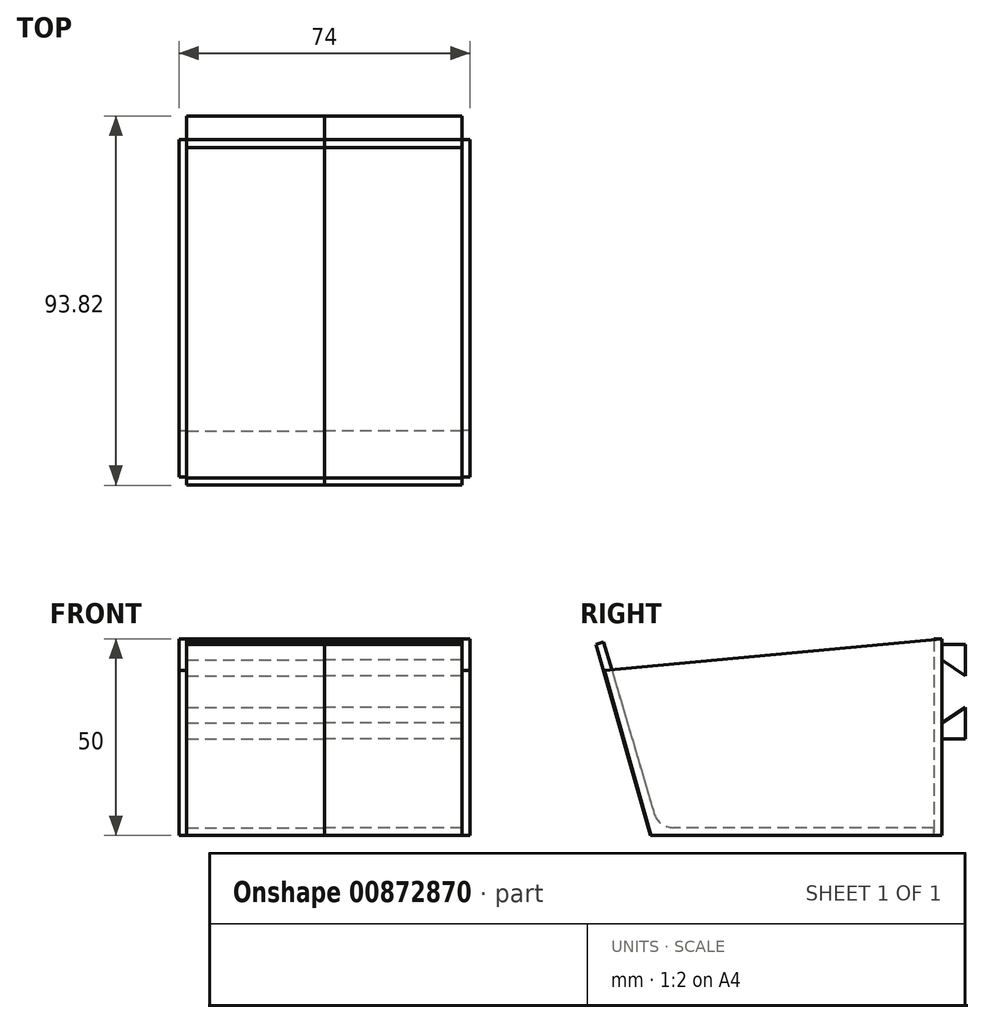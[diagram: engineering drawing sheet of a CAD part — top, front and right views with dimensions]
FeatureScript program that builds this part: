
annotation { "Feature Type Name" : "Feature", "Feature Type Description" : "" }
export const myFeature = defineFeature(function(context is Context, id is Id, definition is map)
    precondition{}
    {
        {
            var Q0;
            Q0=qCreatedBy(makeId("Front.planeOp"),FACE);
            var sketch = newSketch(context, id + "F0", { "sketchPlane" : qUnion([Q0])});
            skLineSegment(sketch, "E0.bottom", {"start": v(-35, 37.16) * mm, "end": v(0, 37.16) * mm});
            skLineSegment(sketch, "E0.top", {"start": v(-35, -12.84) * mm, "end": v(0, -12.84) * mm});
            skLineSegment(sketch, "E0.left", {"start": v(-35, 37.16) * mm, "end": v(-35, -12.84) * mm});
            skLineSegment(sketch, "E0.right", {"start": v(0, 37.16) * mm, "end": v(0, -12.84) * mm});
            skSolve(sketch);
        }
        {
            var Q0;
            Q0=makeQuery(id+"F0.imprint","IMPRINT",FACE,{"disambiguationData":[TD([[makeQuery(id+"F0.imprint","IMPRINT",EDGE,{"derivedFrom":sQuery(id+"F0.wireOp",EDGE,"E0.bottom")}),-1.0]])]});
            extrude(context, id + "F1", {"entities" : qUnion([Q0]), "depth" : 2 * mm, "offsetDistance" : 25 * mm});
        }
        {
            var Q0;
            Q0=qCreatedBy(makeId("Right.planeOp"),FACE);
            var sketch = newSketch(context, id + "F2", { "sketchPlane" : qUnion([Q0])});
            skLineSegment(sketch, "E1", {"start": v(0, 35.71) * mm, "end": v(6, 35.71) * mm});
            skLineSegment(sketch, "E2", {"start": v(6, 35.71) * mm, "end": v(6, 27.71) * mm});
            skLineSegment(sketch, "E3", {"start": v(6, 27.71) * mm, "end": v(0, 31.71) * mm});
            skLineSegment(sketch, "E4", {"start": v(6, 19.71) * mm, "end": v(6, 11.71) * mm});
            skLineSegment(sketch, "E5", {"start": v(6, 11.71) * mm, "end": v(0, 11.71) * mm});
            skLineSegment(sketch, "E6", {"start": v(6, 19.71) * mm, "end": v(0, 15.71) * mm});
            skLineSegment(sketch, "E7", {"start": v(0, 35.71) * mm, "end": v(0, 31.71) * mm});
            skLineSegment(sketch, "E8", {"start": v(0, 15.71) * mm, "end": v(0, 11.71) * mm});
            skLineSegment(sketch, "E9.bottom", {"start": v(-2, -12.84) * mm, "end": v(-72, -12.84) * mm});
            skLineSegment(sketch, "E9.top", {"start": v(-2, -10.84) * mm, "end": v(-68.26, -10.84) * mm});
            skLineSegment(sketch, "E9.left", {"start": v(-2, -12.84) * mm, "end": v(-2, -10.84) * mm});
            skLineSegment(sketch, "E9.right", {"start": v(-72, -12.84) * mm, "end": v(-72, -10.84) * mm});
            skLineSegment(sketch, "E10", {"start": v(-87.82, 35.71) * mm, "end": v(-85.91, 36.33) * mm});
            skLineSegment(sketch, "E11", {"start": v(-85.91, 36.33) * mm, "end": v(-73.06, -7.26) * mm});
            skLineSegment(sketch, "E12", {"start": v(-72, -12.84) * mm, "end": v(-74, -12.84) * mm});
            skLineSegment(sketch, "E13", {"start": v(-87.82, 35.71) * mm, "end": v(-74, -12.84) * mm});
            skPoint(sketch, "E14.visualSharp", {"position": v(-72, -10.84) * mm});
            skArc(sketch, "E14.filletArc", {"start": v(-73.06, -7.26) * mm, "mid": v(-71.26, -9.85) * mm, "end": v(-68.26, -10.84) * mm});
            skSolve(sketch);
        }
        {
            var Q0;
            Q0 = qSketchRegion(id + "F2", true);
            extrude(context, id + "F3", {"entities" : qUnion([Q0]), "oppositeDirection" : true, "depth" : 35 * mm, "offsetDistance" : 25 * mm});
        }
        {
            var Q0;
            Q0=makeQuery(id+"F1.opExtrude","SWEPT_FACE",FACE,{"disambiguationData":[OSD([sQuery(id+"F0.wireOp",EDGE,"E0.left")])]});
            var sketch = newSketch(context, id + "F4", { "sketchPlane" : qUnion([Q0])});
            skLineSegment(sketch, "E15", {"start": v(0, 37.16) * mm, "end": v(0, -12.84) * mm});
            skLineSegment(sketch, "E16", {"start": v(0, -12.84) * mm, "end": v(73.88, -12.84) * mm});
            skLineSegment(sketch, "E17", {"start": v(73.88, -12.84) * mm, "end": v(85.68, 29.12) * mm});
            skLineSegment(sketch, "E18", {"start": v(85.68, 29.12) * mm, "end": v(0, 37.16) * mm});
            skSolve(sketch);
        }
        {
            var Q0;
            Q0 = qSketchRegion(id + "F4", true);
            extrude(context, id + "F5", {"entities" : qUnion([Q0]), "depth" : 2 * mm, "offsetDistance" : 25 * mm});
        }
        {
            var Q0;
            Q0=makeQuery(id+"F5.opExtrude","SWEPT_BODY",BODY,{"disambiguationData":[OSD([sQuery(id+"F4.wireOp",EDGE,"E15"),sQuery(id+"F4.wireOp",EDGE,"E16"),sQuery(id+"F4.wireOp",EDGE,"E17"),sQuery(id+"F4.wireOp",EDGE,"E18")])]});
            var Q1;
            Q1=makeQuery(id+"F3.opExtrude","SWEPT_BODY",BODY,{"disambiguationData":[OSD([sQuery(id+"F2.wireOp",EDGE,"E4"),sQuery(id+"F2.wireOp",EDGE,"E5"),sQuery(id+"F2.wireOp",EDGE,"E6"),sQuery(id+"F2.wireOp",EDGE,"E8")])]});
            var Q2;
            Q2=makeQuery(id+"F3.opExtrude","SWEPT_BODY",BODY,{"disambiguationData":[OSD([sQuery(id+"F2.wireOp",EDGE,"E9.bottom"),sQuery(id+"F2.wireOp",EDGE,"E9.top"),sQuery(id+"F2.wireOp",EDGE,"E9.left"),sQuery(id+"F2.wireOp",EDGE,"E10"),sQuery(id+"F2.wireOp",EDGE,"E11"),sQuery(id+"F2.wireOp",EDGE,"E12"),sQuery(id+"F2.wireOp",EDGE,"E13"),sQuery(id+"F2.wireOp",EDGE,"E14.filletArc")])]});
            var Q3;
            Q3=makeQuery(id+"F3.opExtrude","SWEPT_BODY",BODY,{"disambiguationData":[OSD([sQuery(id+"F2.wireOp",EDGE,"E1"),sQuery(id+"F2.wireOp",EDGE,"E2"),sQuery(id+"F2.wireOp",EDGE,"E3"),sQuery(id+"F2.wireOp",EDGE,"E7")])]});
            var Q4;
            Q4=makeQuery(id+"F1.opExtrude","SWEPT_BODY",BODY,{"disambiguationData":[OSD([sQuery(id+"F0.wireOp",EDGE,"E0.bottom"),sQuery(id+"F0.wireOp",EDGE,"E0.top"),sQuery(id+"F0.wireOp",EDGE,"E0.left"),sQuery(id+"F0.wireOp",EDGE,"E0.right")])]});
            var Q5;
            Q5=qCreatedBy(makeId("Right.planeOp"),FACE);
            mirror(context, id + "F6", {"entities" : qUnion([Q0, Q1, Q2, Q3, Q4]), "mirrorPlane" : qUnion([Q5])});
        }
    });
